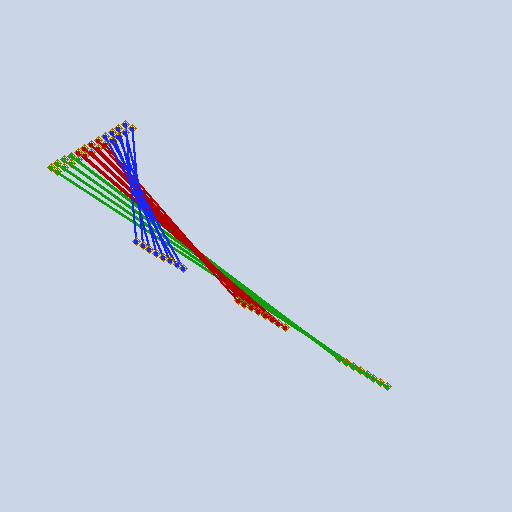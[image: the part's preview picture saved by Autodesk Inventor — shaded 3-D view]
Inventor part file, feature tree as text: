
AUTODESK INVENTOR PART (.ipt)
format: ipt  version: 2023.1 (Build 271208000, 208)  size: 216,064 bytes
history: native  units: mm (DEFAULTED — no unit token found)
features: other x96, plane x24, sketch x24, sweep x24
ambient origin geometry x8: Origin, YZ Plane, XZ Plane, XY Plane, X Axis, Y Axis, Z Axis, Center Point
feature tree (168):
  other  "Work Point1"
  other  "Work Point2"
  other  "Wire1"
  other  "Work Point3"
  other  "Work Point4"
  other  "Wire2"
  other  "Work Point5"
  other  "Work Point6"
  other  "Wire3"
  other  "Work Point7"
  other  "Work Point8"
  other  "Wire4"
  other  "Work Point9"
  other  "Work Point10"
  other  "Wire5"
  other  "Work Point11"
  other  "Work Point12"
  other  "Wire6"
  other  "Work Point13"
  other  "Work Point14"
  other  "Wire7"
  other  "Work Point15"
  other  "Work Point16"
  other  "Wire8"
  other  "Work Point17"
  other  "Work Point18"
  other  "Wire9"
  other  "Work Point19"
  other  "Work Point20"
  other  "Wire10"
  other  "Work Point21"
  other  "Work Point22"
  other  "Wire11"
  other  "Work Point23"
  other  "Work Point24"
  other  "Wire12"
  other  "Work Point25"
  other  "Work Point26"
  other  "Wire13"
  other  "Work Point27"
  other  "Work Point28"
  other  "Wire14"
  other  "Work Point29"
  other  "Work Point30"
  other  "Wire15"
  other  "Work Point31"
  other  "Work Point32"
  other  "Wire16"
  other  "Work Point33"
  other  "Work Point34"
  other  "Wire17"
  other  "Work Point35"
  other  "Work Point36"
  other  "Wire18"
  other  "Work Point37"
  other  "Work Point38"
  other  "Wire19"
  other  "Work Point39"
  other  "Work Point40"
  other  "Wire20"
  other  "Work Point41"
  other  "Work Point42"
  other  "Wire21"
  other  "Work Point43"
  other  "Work Point44"
  other  "Wire22"
  other  "Work Point45"
  other  "Work Point46"
  other  "Wire23"
  other  "Work Point47"
  other  "Work Point48"
  other  "Wire24"
  plane  "Work Plane1"
  plane  "Work Plane2"
  plane  "Work Plane3"
  plane  "Work Plane4"
  plane  "Work Plane5"
  plane  "Work Plane6"
  plane  "Work Plane7"
  plane  "Work Plane8"
  plane  "Work Plane9"
  plane  "Work Plane10"
  plane  "Work Plane11"
  plane  "Work Plane12"
  plane  "Work Plane13"
  plane  "Work Plane14"
  plane  "Work Plane15"
  plane  "Work Plane16"
  plane  "Work Plane17"
  plane  "Work Plane18"
  plane  "Work Plane19"
  plane  "Work Plane20"
  plane  "Work Plane21"
  plane  "Work Plane22"
  plane  "Work Plane23"
  plane  "Work Plane24"
  sketch  "Sketch1"  dims[d0=0.0mm d1=0.0mm d2=0.0mm d3=0.0mm]
  other  "Srf1"
  sketch  "Sketch2"  dims[d4=0.0mm d5=0.0mm d6=0.0mm d7=0.0mm]
  other  "Srf2"
  sketch  "Sketch3"  dims[d8=0.0mm d9=0.0mm d10=0.0mm d11=0.0mm]
  other  "Srf3"
  sketch  "Sketch4"  dims[d12=0.0mm d13=0.0mm d14=0.0mm d15=0.0mm]
  other  "Srf4"
  sketch  "Sketch5"  dims[d16=0.0mm d17=0.0mm d18=0.0mm d19=0.0mm]
  other  "Srf5"
  sketch  "Sketch6"  dims[d20=0.0mm d21=0.0mm d22=0.0mm d23=0.0mm]
  other  "Srf6"
  sketch  "Sketch7"  dims[d24=0.0mm d25=0.0mm d26=0.0mm d27=0.0mm]
  other  "Srf7"
  sketch  "Sketch8"  dims[d28=0.0mm d29=0.0mm d30=0.0mm d31=0.0mm]
  other  "Srf8"
  sketch  "Sketch9"  dims[d32=0.0mm d33=0.0mm d34=0.0mm d35=0.0mm]
  other  "Srf9"
  sketch  "Sketch10"  dims[d36=0.0mm d37=0.0mm d38=0.0mm d39=0.0mm]
  other  "Srf10"
  sketch  "Sketch11"  dims[d40=0.0mm d41=0.0mm d42=0.0mm d43=0.0mm]
  other  "Srf11"
  sketch  "Sketch12"  dims[d44=0.0mm d45=0.0mm d46=0.0mm d47=0.0mm]
  other  "Srf12"
  sketch  "Sketch13"
  other  "Srf13"
  sketch  "Sketch14"
  other  "Srf14"
  sketch  "Sketch15"
  other  "Srf15"
  sketch  "Sketch16"
  other  "Srf16"
  sketch  "Sketch17"
  other  "Srf17"
  sketch  "Sketch18"
  other  "Srf18"
  sketch  "Sketch19"
  other  "Srf19"
  sketch  "Sketch20"
  other  "Srf20"
  sketch  "Sketch21"
  other  "Srf21"
  sketch  "Sketch22"
  other  "Srf22"
  sketch  "Sketch23"
  other  "Srf23"
  sketch  "Sketch24"
  other  "Srf24"
  sweep  "SweepSrf1"
  sweep  "SweepSrf2"
  sweep  "SweepSrf3"
  sweep  "SweepSrf4"
  sweep  "SweepSrf5"
  sweep  "SweepSrf6"
  sweep  "SweepSrf7"
  sweep  "SweepSrf8"
  sweep  "SweepSrf9"
  sweep  "SweepSrf10"
  sweep  "SweepSrf11"
  sweep  "SweepSrf12"
  sweep  "SweepSrf13"
  sweep  "SweepSrf14"
  sweep  "SweepSrf15"
  sweep  "SweepSrf16"
  sweep  "SweepSrf17"
  sweep  "SweepSrf18"
  sweep  "SweepSrf19"
  sweep  "SweepSrf20"
  sweep  "SweepSrf21"
  sweep  "SweepSrf22"
  sweep  "SweepSrf23"
  sweep  "SweepSrf24"
